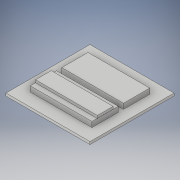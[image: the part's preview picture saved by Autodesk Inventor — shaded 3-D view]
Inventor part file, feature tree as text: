
AUTODESK INVENTOR PART (.ipt)
format: ipt  version: 2019.4 (Build 234330000, 330)  size: 134,144 bytes
history: native  units: in
note: dims shown in document units (in); Inventor stores cm internally (conversion verified against a paired STEP export)
features: extrude x3, sketch x3, projected_geometry x1
ambient origin geometry x8: Origin, YZ Plane, XZ Plane, XY Plane, X Axis, Y Axis, Z Axis, Center Point
bodies: Solid1 (feature_tree)
feature tree (7):
  extrude  "Extrusion1"  Depth=8.0in
  extrude  "Extrusion2"  Depth=0.25in TaperAngle=0.0deg
  extrude  "Extrusion3"  Depth=2.5in
  sketch  "Sketch1"  dims[d0=8.0in d1=4.0in]
  sketch  "Sketch2"  dims[d2=4.0in d3=0.25in d4=0.0in]
  projected_geometry  "Projected Loop1"
  sketch  "Sketch3"  dims[d5=5.875in d6=2.5in d7=1.0625in d8=1.25in d9=2.5in d10=1.25in d11=0.5in d12=0.0in d13=1.5in d14=0.5in d15=0.25in d16=0.0in]
